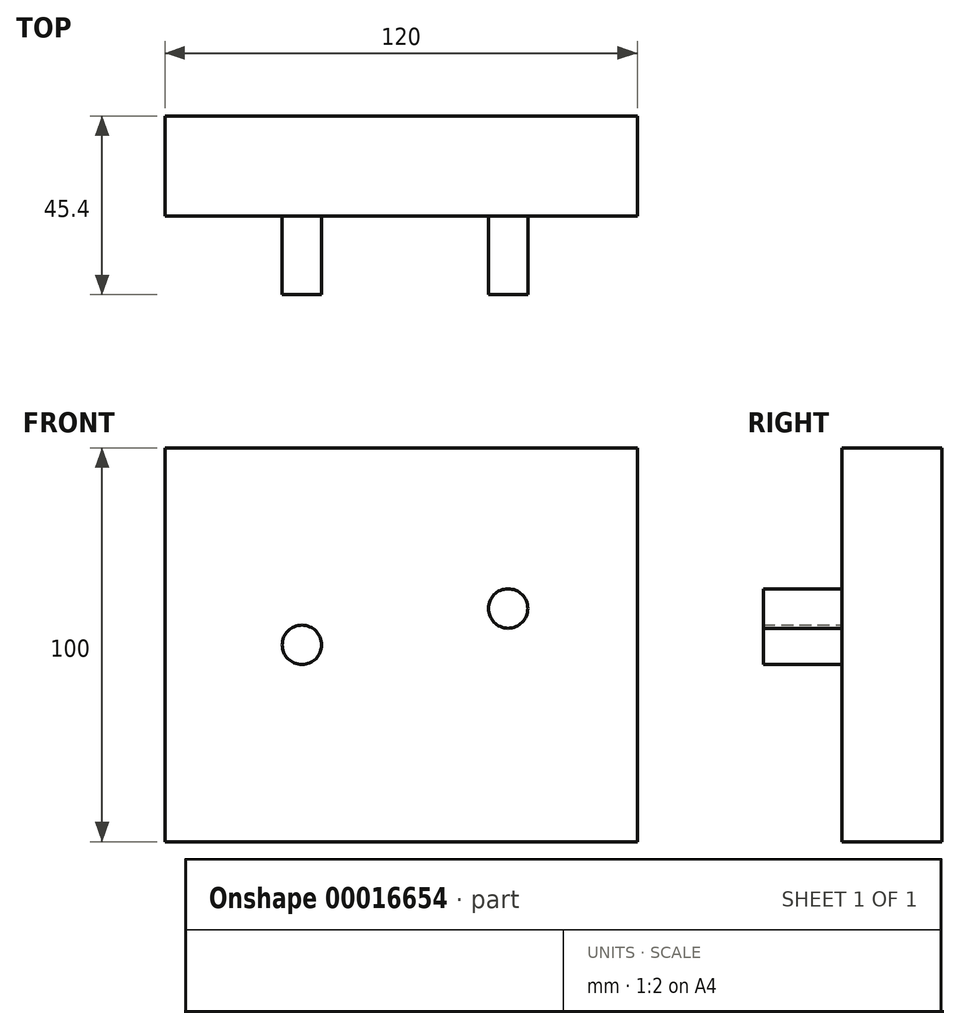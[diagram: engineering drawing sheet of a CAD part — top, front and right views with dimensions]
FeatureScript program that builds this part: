
annotation { "Feature Type Name" : "Feature", "Feature Type Description" : "" }
export const myFeature = defineFeature(function(context is Context, id is Id, definition is map)
    precondition{}
    {
        {
            var Q0;
            Q0=qCreatedBy(makeId("Front.planeOp"),FACE);
            var sketch = newSketch(context, id + "F0", { "sketchPlane" : qUnion([Q0])});
            skLineSegment(sketch, "E0.rect.bottom", {"start": v(60, 50) * mm, "end": v(-60, 50) * mm});
            skLineSegment(sketch, "E0.rect.top", {"start": v(60, -50) * mm, "end": v(-60, -50) * mm});
            skLineSegment(sketch, "E0.rect.left", {"start": v(60, 50) * mm, "end": v(60, -50) * mm});
            skLineSegment(sketch, "E0.rect.right", {"start": v(-60, 50) * mm, "end": v(-60, -50) * mm});
            skPoint(sketch, "E0.rect.middle", {"position": v(0, 0) * mm});
            skSolve(sketch);
        }
        {
            var Q0;
            Q0 = qSketchRegion(id + "F0", true);
            extrude(context, id + "F1", {"entities" : qUnion([Q0]), "depth" : 25.4 * mm});
        }
        {
            var Q0;
            Q0=makeQuery(id+"F1.opExtrude","CAP_FACE",FACE,{"disambiguationData":[OSD([sQuery(id+"F0.wireOp",EDGE,"E0.rect.bottom"),sQuery(id+"F0.wireOp",EDGE,"E0.rect.top"),sQuery(id+"F0.wireOp",EDGE,"E0.rect.left"),sQuery(id+"F0.wireOp",EDGE,"E0.rect.right")])],"isStart":false});
            var sketch = newSketch(context, id + "F2", { "sketchPlane" : qUnion([Q0])});
            skCircle(sketch, "E1", {"center": v(-25.21, 0) * mm, "radius": 5 * mm});
            skCircle(sketch, "E2", {"center": v(27.17, 9.23) * mm, "radius": 5 * mm});
            skSolve(sketch);
        }
        {
            var Q0;
            Q0 = qSketchRegion(id + "F2", true);
            extrude(context, id + "F3", {"entities" : qUnion([Q0]), "operationType" : NewBodyOperationType.ADD, "depth" : 20 * mm});
        }
    });
